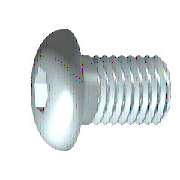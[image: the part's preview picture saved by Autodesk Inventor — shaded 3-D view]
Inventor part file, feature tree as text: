
AUTODESK INVENTOR PART (.ipt)
format: ipt  version: 2014 (Build 180170000, 170)  size: 197,120 bytes
history: native  units: mm (DEFAULTED — no unit token found)
features: sketch x2, extrude x1, plane x1, fillet x1
ambient origin geometry x7: Origin, YZ Plane, XY Plane, X Axis, Y Axis, Z Axis, Center Point
bodies: Solid1 (feature_tree), Body (feature_tree)
feature tree (5):
  extrude  "Slot"  Depth=1.8542mm
  plane  "Work Plane1"
  fillet  "Fillet2"  Radius=1.8542mm
  sketch  "Sketch1"  dims[d1=4.75976mm d2=1.59014mm d3=1.8542mm]
  sketch  "Sketch2"  dims[d4=1.1176mm d5=60.0deg d6=3.5052mm d7=3.5052mm d8=2.287693mm d9=6.6548mm d10=90.0deg d11=10.0mm d12=0.0mm d13=4.75976mm d14=0.0mm d15=0.486918mm d16=0.486918mm d17=1.6002mm d19=0.0mm d26=6.35mm d27=45.0deg d28=0.0mm d29=0.0mm d30=0.1mm]
